# Revit family: GC5
name_source: partatom
category: Furniture
units: mm (PartAtom-declared; Revit-internal decimal feet)

## family parameters
Always vertical = Yes
Cut with Voids When Loaded = No
OmniClass Number = 23.40.00.00
OmniClass Title = Equipment and Furnishings
Room Calculation Point = No
Shared = No
Work Plane-Based = No

## types (4) — shared parameters
Assembly Code = E2020200
Base = Gresham - GREY PLASTIC
Manufacturer = Gresham Office Funiture
Model = GC5
Product Brochure = https://gof.co.uk
Product Data Specification = https://gof.co.uk
Range = SEATING
Tablet = Gresham - BLACK PLASTIC
Tablet Support = Gresham - GREY METAL
URL = www.gof.co.uk

## per-type parameters (varying)
| type | Product Code | Tablet (vis) | Upholstered Seat | Upholstered Seat Pad |
| GC5A1 | GC5A1 | No | GABRIEL Byron_11101 | No |
| GC5A2 | GC5A2 | No | GABRIEL Byron_11101 | Yes |
| GC5B1 | GC5B1 | Yes | GABRIEL Byron_11101 | No |
| GCGB2 | GC5B2 | Yes | GABRIEL Byron_14101 | Yes |

## geometry (parser evidence)
native form markers: Sweep x2
no freeform markers — native parametric forms only
